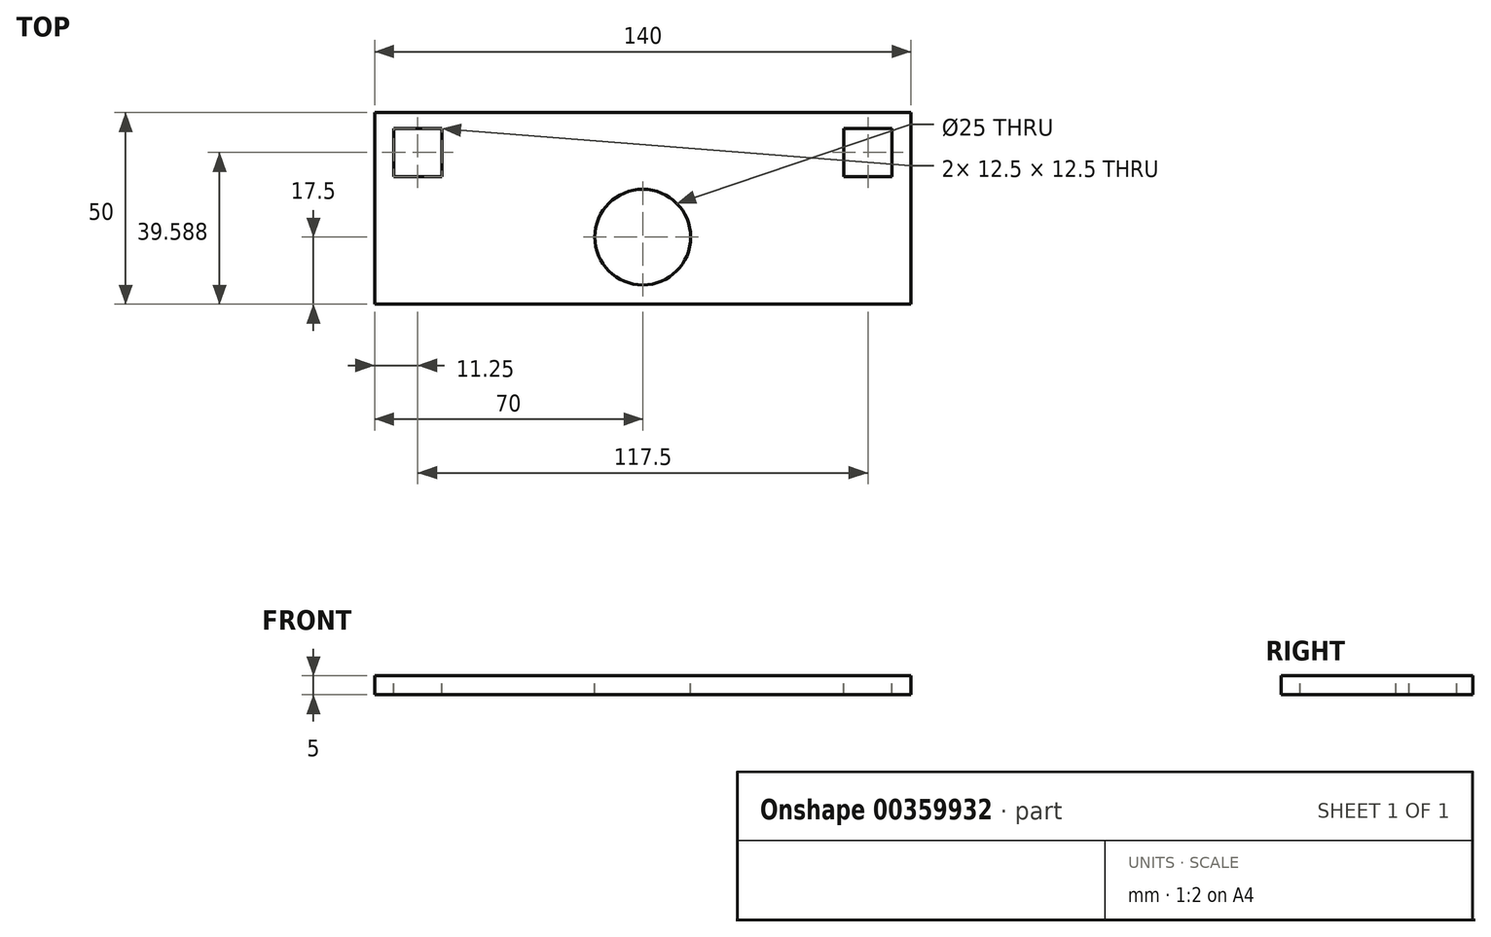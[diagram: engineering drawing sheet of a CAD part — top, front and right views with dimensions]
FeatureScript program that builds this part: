
annotation { "Feature Type Name" : "Feature", "Feature Type Description" : "" }
export const myFeature = defineFeature(function(context is Context, id is Id, definition is map)
    precondition{}
    {
        {
            var Q0;
            Q0=qCreatedBy(makeId("Top.planeOp"),FACE);
            var sketch = newSketch(context, id + "F0", { "sketchPlane" : qUnion([Q0])});
            skLineSegment(sketch, "E0.bottom", {"start": v(-67.77, 20.9) * mm, "end": v(72.23, 20.9) * mm});
            skLineSegment(sketch, "E0.top", {"start": v(-67.77, -29.1) * mm, "end": v(72.23, -29.1) * mm});
            skLineSegment(sketch, "E0.left", {"start": v(-67.77, 20.9) * mm, "end": v(-67.77, -29.1) * mm});
            skLineSegment(sketch, "E0.right", {"start": v(72.23, 20.9) * mm, "end": v(72.23, -29.1) * mm});
            skSolve(sketch);
        }
        {
            var Q0;
            Q0=makeQuery(id+"F0.imprint","IMPRINT",FACE,{"disambiguationData":[TD([[makeQuery(id+"F0.imprint","IMPRINT",EDGE,{"derivedFrom":sQuery(id+"F0.wireOp",EDGE,"E0.bottom")}),-1.0]])]});
            extrude(context, id + "F1", {"entities" : qUnion([Q0]), "depth" : 5 * mm});
        }
        {
            var Q0;
            Q0=makeQuery(id+"F1.opExtrude","CAP_FACE",FACE,{"disambiguationData":[OSD([sQuery(id+"F0.wireOp",EDGE,"E0.bottom"),sQuery(id+"F0.wireOp",EDGE,"E0.top"),sQuery(id+"F0.wireOp",EDGE,"E0.left"),sQuery(id+"F0.wireOp",EDGE,"E0.right")])],"isStart":false});
            var sketch = newSketch(context, id + "F2", { "sketchPlane" : qUnion([Q0])});
            skLineSegment(sketch, "E1.bottom", {"start": v(-62.77, 16.75) * mm, "end": v(-50.27, 16.75) * mm});
            skLineSegment(sketch, "E1.top", {"start": v(-62.77, 4.25) * mm, "end": v(-50.27, 4.25) * mm});
            skLineSegment(sketch, "E1.left", {"start": v(-62.77, 16.75) * mm, "end": v(-62.77, 4.25) * mm});
            skLineSegment(sketch, "E1.right", {"start": v(-50.27, 16.75) * mm, "end": v(-50.27, 4.25) * mm});
            skLineSegment(sketch, "E2", {"start": v(2.23, -29.1) * mm, "end": v(2.23, 20.9) * mm, "construction": true});
            skLineSegment(sketch, "E3.MirrorCS", {"start": v(54.73, 16.75) * mm, "end": v(54.73, 4.25) * mm});
            skLineSegment(sketch, "E4.MirrorCS", {"start": v(67.23, 16.75) * mm, "end": v(67.23, 4.25) * mm});
            skLineSegment(sketch, "E5.MirrorCS", {"start": v(67.23, 4.25) * mm, "end": v(54.73, 4.25) * mm});
            skLineSegment(sketch, "E6.MirrorCS", {"start": v(67.23, 16.75) * mm, "end": v(54.73, 16.75) * mm});
            skSolve(sketch);
        }
        {
            var Q0;
            Q0=makeQuery(id+"F2.imprint","IMPRINT",FACE,{"disambiguationData":[TD([[makeQuery(id+"F2.imprint","IMPRINT",EDGE,{"derivedFrom":sQuery(id+"F2.wireOp",EDGE,"E1.bottom")}),-1.0]])]});
            var Q1;
            Q1=makeQuery(id+"F2.imprint","IMPRINT",FACE,{"disambiguationData":[TD([[makeQuery(id+"F2.imprint","IMPRINT",EDGE,{"derivedFrom":sQuery(id+"F2.wireOp",EDGE,"E3.MirrorCS")}),1.0]])]});
            extrude(context, id + "F3", {"entities" : qUnion([Q0, Q1]), "operationType" : NewBodyOperationType.REMOVE, "oppositeDirection" : true, "depth" : 25 * mm});
        }
        {
            var Q0;
            Q0=makeQuery(id+"F1.opExtrude","CAP_FACE",FACE,{"disambiguationData":[OSD([sQuery(id+"F0.wireOp",EDGE,"E0.bottom"),sQuery(id+"F0.wireOp",EDGE,"E0.top"),sQuery(id+"F0.wireOp",EDGE,"E0.left"),sQuery(id+"F0.wireOp",EDGE,"E0.right")])],"isStart":false});
            var sketch = newSketch(context, id + "F4", { "sketchPlane" : qUnion([Q0])});
            skLineSegment(sketch, "E7", {"start": v(2.23, 20.9) * mm, "end": v(2.23, -29.1) * mm, "construction": true});
            skCircle(sketch, "E8", {"center": v(2.23, -11.6) * mm, "radius": 12.5 * mm});
            skSolve(sketch);
        }
        {
            var Q0;
            Q0=makeQuery(id+"F4.imprint","IMPRINT",FACE,{"disambiguationData":[TD([[makeQuery(id+"F4.imprint","IMPRINT",EDGE,{"derivedFrom":sQuery(id+"F4.wireOp",EDGE,"E8")}),1.0]])]});
            extrude(context, id + "F5", {"entities" : qUnion([Q0]), "operationType" : NewBodyOperationType.REMOVE, "oppositeDirection" : true, "depth" : 25 * mm});
        }
    });
